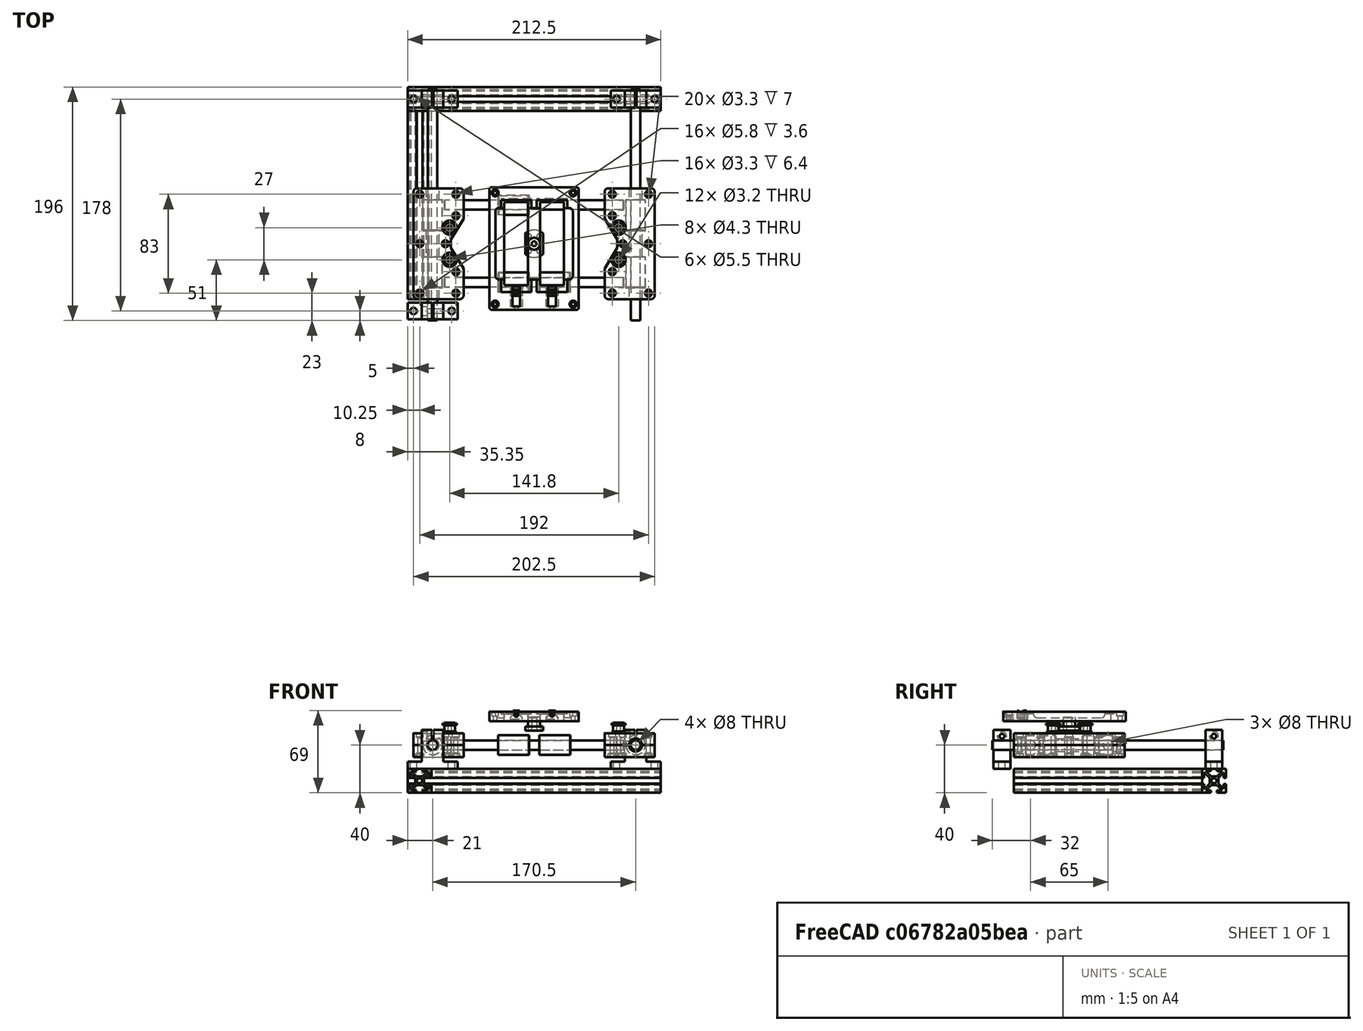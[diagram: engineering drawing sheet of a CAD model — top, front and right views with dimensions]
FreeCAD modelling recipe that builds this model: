
FCSTD DOCUMENT  (FreeCAD 0.16R6706 (Git))
Label: stage3_sh8_alu20
License: All rights reserved
LicenseURL: http://en.wikipedia.org/wiki/All_rights_reserved
objects: Part::FeaturePython×33, Part::Prism×20, Part::Feature×20, Part::Cylinder×19, Part::Extrusion×13, Part::Circle×11, Part::Cut×10, Part::MultiFuse×9, Part::Box×8, Part::Common×6, Part::Compound×5, Part::Fillet×4, Part::Fuse×4, Part::Polygon×2
note: 164 computed .brp shape members not serialized (recipe doc carries the construction recipe); baked Part::Feature solids carry a one-line shape summary decoded from their .brp

FEATURE [Part::Box] topsideslid_box
  Height = 10
  Length = 42
  Placement = pos=(-16,-46.5,0) rot=(0,0,1;0rad)
  Width = 93
FEATURE [Part::Box] bosidetslid_box
  Height = 10
  Length = 42
  Placement = pos=(-16,-46.5,-10) rot=(0,0,1;0rad)
  Width = 93
FEATURE [Part::Fillet] topsideslid_fllt
  Base = -> topsideslid_box
  Edges = 4 edges r=3: [Edge1,Edge3,Edge5,Edge7]
FEATURE [Part::Fillet] botsideslid_fllt
  Base = -> bosidetslid_box
  Edges = 4 edges r=3: [Edge1,Edge3,Edge5,Edge7]
FEATURE [Part::Circle] sliderod_circ
  Angle0 = 0
  Angle1 = 360
  Placement = pos=(0,-47.5,0) rot=(-1,0,0;1.5708rad)
  Radius = 5.5
FEATURE [Part::Extrusion] sliderod
  Base = -> sliderod_circ
  Dir = (0,95,0)
  Solid = true
FEATURE [Part::Cylinder] lm8uu_0_ext
  Angle = 360
  Height = 25
  Placement = pos=(0,-36.5,0) rot=(-1,0,0;1.5708rad)
  Radius = 8
FEATURE [Part::Cylinder] lm8uu_0_int
  Angle = 360
  Height = 27
  Placement = pos=(0,-37.5,0) rot=(-1,0,0;1.5708rad)
  Radius = 4
FEATURE [Part::Cut] lm8uu_0
  Base = -> lm8uu_0_ext
  Tool = -> lm8uu_0_int
FEATURE [Part::Circle] lm8uu_0_cont_circ
  Angle0 = 0
  Angle1 = 360
  Placement = pos=(0,-37,0) rot=(-1,0,0;1.5708rad)
  Radius = 8.35
FEATURE [Part::Extrusion] lm8uu_0_cont
  Base = -> lm8uu_0_cont_circ
  Dir = (0,26,0)
  Solid = true
FEATURE [Part::FeaturePython] Clone  label="lm8uu_1"  # Draft clone (typed FeaturePython)
  Objects = -> [lm8uu_0]
  Placement = pos=(0,48,0) rot=(0,0,1;0rad)
  Scale = (1,1,1)
FEATURE [Part::FeaturePython] Clone001  label="lm8uu_1_cont"  # Draft clone (typed FeaturePython)
  Objects = -> [lm8uu_0_cont]
  Placement = pos=(0,48,0) rot=(0,0,1;0rad)
  Scale = (1,1,1)
FEATURE [Part::Circle] holdrod_0_circ
  Angle0 = 0
  Angle1 = 360
  Placement = pos=(10,0,0) rot=(0,1,0;1.5708rad)
  Radius = 4.175
FEATURE [Part::Extrusion] holdrod_0
  Base = -> holdrod_0_circ
  Dir = (17,0,0)
  Placement = pos=(0,-32.5,0) rot=(0,0,1;0rad)
  Solid = true
FEATURE [Part::Circle] holdrod_1_circ
  Angle0 = 0
  Angle1 = 360
  Placement = pos=(10,0,0) rot=(0,1,0;1.5708rad)
  Radius = 4.175
FEATURE [Part::Extrusion] holdrod_1
  Base = -> holdrod_1_circ
  Dir = (17,0,0)
  Placement = pos=(0,32.5,0) rot=(0,0,1;0rad)
  Solid = true
FEATURE [Part::Cylinder] bolt_hole_bolt_shank
  Angle = 360
  Height = 22
  Placement = pos=(0,0,-1) rot=(0,0,1;0rad)
  Radius = 1.65
FEATURE [Part::Cylinder] bolt_hole_bolt_head
  Angle = 360
  Height = 4.3
  Placement = pos=(0,0,16.7) rot=(0,0,1;0rad)
  Radius = 2.9
FEATURE [Part::Prism] bolt_hole_bolt_sup1
  Circumradius = 3.3
  Height = 3.6
  Placement = pos=(0,0,16.4) rot=(0,0,1;0.523599rad)
  Polygon = 3
FEATURE [Part::Cylinder] bolt_hole_bolt_sup1away
  Angle = 360
  Height = 3.6
  Placement = pos=(0,0,16.4) rot=(0,0,1;0rad)
  Radius = 2.9
FEATURE [Part::Common] sup1cut
  Base = -> bolt_hole_bolt_sup1
  Tool = -> bolt_hole_bolt_sup1away
FEATURE [Part::Prism] bolt_hole_bolt_sup2
  Circumradius = 1.8975
  Height = 3.9
  Placement = pos=(0,0,16.1) rot=(0,0,1;0rad)
  Polygon = 6
FEATURE [Part::MultiFuse] bolt_hole_bolt
  Shapes = -> [bolt_hole_bolt_shank,bolt_hole_bolt_head,sup1cut,bolt_hole_bolt_sup2]
FEATURE [Part::Prism] bolt_hole_nut
  Circumradius = 3.455
  Height = 3.7
  Placement = pos=(0,0,-1) rot=(0,0,1;0rad)
  Polygon = 6
FEATURE [Part::Prism] bolt_hole_nutsup1
  Circumradius = 3.3
  Height = 3
  Placement = pos=(0,0,0) rot=(0,0,1;0.523599rad)
  Polygon = 3
FEATURE [Part::Prism] bolt_hole_supnut1away
  Circumradius = 3.455
  Height = 3
  Polygon = 6
FEATURE [Part::Common] supnut1_cut
  Base = -> bolt_hole_nutsup1
  Tool = -> bolt_hole_supnut1away
FEATURE [Part::Prism] bolt_hole_supnut2
  Circumradius = 1.8975
  Height = 3.3
  Polygon = 6
FEATURE [Part::MultiFuse] boltnut
  Placement = pos=(-10.75,0,-10) rot=(0,0,1;1.5708rad)
  Shapes = -> [bolt_hole_bolt,bolt_hole_nut,supnut1_cut,bolt_hole_supnut2]
FEATURE [Part::FeaturePython] Clone002  label="bolt_hole_r"  # Draft clone (typed FeaturePython)
  Objects = -> [boltnut]
  Placement = pos=(10.75,0,-10) rot=(0,0,1;0.523599rad)
  Scale = (1,1,1)
FEATURE [Part::FeaturePython] Clone003  label="bolt_hole_lu"  # Draft clone (typed FeaturePython)
  Objects = -> [boltnut]
  Placement = pos=(-10.75,-41.5,-10) rot=(0,0,1;0rad)
  Scale = (1,1,1)
FEATURE [Part::FeaturePython] Clone004  label="bolt_hole_ld"  # Draft clone (typed FeaturePython)
  Objects = -> [boltnut]
  Placement = pos=(-10.75,41.5,-10) rot=(0,0,1;0rad)
  Scale = (1,1,1)
FEATURE [Part::FeaturePython] Clone005  label="bolt_hole_ru"  # Draft clone (typed FeaturePython)
  Objects = -> [boltnut]
  Placement = pos=(19.6,41.5,-10) rot=(0,0,1;0rad)
  Scale = (1,1,1)
FEATURE [Part::FeaturePython] Clone006  label="bolt_hole_rd"  # Draft clone (typed FeaturePython)
  Objects = -> [boltnut]
  Placement = pos=(19.6,-41.5,-10) rot=(0,0,1;0rad)
  Scale = (1,1,1)
FEATURE [Part::FeaturePython] Clone007  label="bolt_hole_rmu"  # Draft clone (typed FeaturePython)
  Objects = -> [boltnut]
  Placement = pos=(19.6,23.5,-10) rot=(0,0,1;0rad)
  Scale = (1,1,1)
FEATURE [Part::FeaturePython] Clone008  label="bolt_hole_rmd"  # Draft clone (typed FeaturePython)
  Objects = -> [boltnut]
  Placement = pos=(19.6,-23.5,-10) rot=(0,0,1;0rad)
  Scale = (1,1,1)
FEATURE [Part::Cylinder] boltpul_hole_shank
  Angle = 360
  Height = 22
  Placement = pos=(0,0,-1) rot=(0,0,1;0rad)
  Radius = 1.65
FEATURE [Part::Prism] boltpul_hole_head
  Circumradius = 3.455
  Height = 3.7
  Placement = pos=(0,0,-1) rot=(0,0,1;0rad)
  Polygon = 6
FEATURE [Part::Prism] boltpul_hole_sup1
  Circumradius = 3.3
  Height = 3
  Placement = pos=(0,0,0) rot=(0,0,1;0.523599rad)
  Polygon = 3
FEATURE [Part::Prism] boltpul_hole_sup1away
  Circumradius = 3.455
  Height = 3
  Polygon = 6
FEATURE [Part::Common] sup1cut001
  Base = -> boltpul_hole_sup1
  Tool = -> boltpul_hole_sup1away
FEATURE [Part::Prism] boltpul_hole_sup2
  Circumradius = 1.8975
  Height = 3.3
  Polygon = 6
FEATURE [Part::MultiFuse] boltpul_hole
  Placement = pos=(14.35,13.5,-10) rot=(0,0,1;0.523599rad)
  Shapes = -> [boltpul_hole_shank,boltpul_hole_head,sup1cut001,boltpul_hole_sup2]
FEATURE [Part::Feature] idlepull_01
  shape: bbox 12 x 12 x 1 mm, 4 faces (baked)
FEATURE [Part::Feature] idlepull_02
  shape: bbox 7 x 7 x 0.5 mm, 4 faces (baked)
FEATURE [Part::Feature] idlepull_03
  shape: bbox 9 x 9 x 5 mm, 4 faces (baked)
FEATURE [Part::Feature] idlepull_04
  shape: bbox 7 x 7 x 0.5 mm, 4 faces (baked)
FEATURE [Part::Feature] idlepull_05
  shape: bbox 12 x 12 x 1 mm, 4 faces (baked)
FEATURE [Part::Feature] idlepull_06
  shape: bbox 9 x 9 x 0.8 mm, 4 faces (baked)
FEATURE [Part::Compound] idlepull_0
  Links = -> [idlepull_01,idlepull_02,idlepull_03,idlepull_04,idlepull_05,idlepull_06]
FEATURE [Part::FeaturePython] Clone009  label="boltpul_hole_1"  # Draft clone (typed FeaturePython)
  Objects = -> [boltpul_hole]
  Placement = pos=(14.35,-13.5,-10) rot=(0,0,1;0.523599rad)
  Scale = (1,1,1)
FEATURE [Part::FeaturePython] Clone010  label="idlepull_1"  # Draft clone (typed FeaturePython)
  Objects = -> [idlepull_0]
  Placement = pos=(0,-27,0) rot=(0,0,1;0rad)
  Scale = (1,1,1)
FEATURE [Part::Compound] idlepulls
  Links = -> [idlepull_0,Clone010]
  Placement = pos=(-85.25,0,0) rot=(0,0,1;0rad)
FEATURE [Part::Polygon] dent_plane
  Close = true
  Nodes = (4) [(27,22.5,-11),(15.35,3.5,-11),(15.35,-3.5,-11),(27,-22.5,-11)]
FEATURE [Part::Extrusion] dent
  Base = -> dent_plane
  Dir = (0,0,22)
  Solid = true
FEATURE [Part::MultiFuse] holes
  Shapes = -> [sliderod,lm8uu_0_cont,Clone001,holdrod_0,holdrod_1,boltnut,Clone002,Clone003,Clone004,Clone005,Clone006,Clone007,Clone008,boltpul_hole,Clone009,dent]
FEATURE [Part::Fuse] yslider_nx_bear
  Base = -> lm8uu_0
  Placement = pos=(-85.25,0,0) rot=(0,0,1;0rad)
  Tool = -> Clone
FEATURE [Part::Cut] yslider_nx_top
  Base = -> topsideslid_fllt
  Placement = pos=(-85.25,0,0) rot=(0,0,1;0rad)
  Tool = -> holes
FEATURE [Part::Cut] yslider_nx_bot
  Base = -> botsideslid_fllt
  Placement = pos=(-85.25,0,0) rot=(0,0,1;0rad)
  Tool = -> holes
FEATURE [Part::Feature] alux_y0
  Placement = pos=(0,-56.5,-40) rot=(0,0,1;0rad)
  shape: bbox 212.5 x 20 x 20 mm, 43 faces (baked)
FEATURE [Part::FeaturePython] Clone011  label="alux_y"  # Draft clone (typed FeaturePython)
  Objects = -> [alux_y0]
  Placement = pos=(0,121.5,-40) rot=(0,0,1;0rad)
  Scale = (1,1,1)
FEATURE [Part::Feature] aluy_x
  Placement = pos=(96.25,-46.5,-40) rot=(0,0,1;0rad)
  shape: bbox 20 x 158 x 20 mm, 43 faces (baked)
FEATURE [Part::FeaturePython] Clone012  label="aluy_nx"  # Draft clone (typed FeaturePython)
  Objects = -> [aluy_x]
  Placement = pos=(-96.25,-46.5,-40) rot=(0,0,1;0rad)
  Scale = (1,1,1)
FEATURE [Part::Box] total_box
  Height = 32.8
  Length = 14
  Placement = pos=(0,-21,0) rot=(0,0,1;0rad)
  Width = 42
FEATURE [Part::Box] side_box_r
  Height = 26.8
  Length = 14
  Placement = pos=(0,9,6) rot=(0,0,1;0rad)
  Width = 12
FEATURE [Part::Box] side_box_l
  Height = 26.8
  Length = 14
  Placement = pos=(0,-21,6) rot=(0,0,1;0rad)
  Width = 12
FEATURE [Part::Fuse] side_boxes
  Base = -> side_box_r
  Tool = -> side_box_l
FEATURE [Part::Cut] sk_shape
  Base = -> total_box
  Tool = -> side_boxes
FEATURE [Part::Cylinder] shaft_hole
  Angle = 360
  Height = 16
  Placement = pos=(-1,0,20) rot=(0,1,0;1.5708rad)
  Radius = 4
FEATURE [Part::Box] up_sep
  Height = 13.8
  Length = 16
  Placement = pos=(-1,-0.6,21) rot=(0,0,1;0rad)
  Width = 1.2
FEATURE [Part::Cylinder] tbolt_shaft
  Angle = 360
  Height = 20
  Placement = pos=(7,10,27.5) rot=(1,0,0;1.5708rad)
  Radius = 2
FEATURE [Part::Cylinder] tbolt_head
  Angle = 360
  Height = 5.4
  Placement = pos=(7,10,27.5) rot=(1,0,0;1.5708rad)
  Radius = 3.85
FEATURE [Part::MultiFuse] fuse_shaft_holes
  Shapes = -> [tbolt_head,tbolt_shaft,up_sep,shaft_hole]
FEATURE [Part::Cut] sk_shape_w_holes
  Base = -> sk_shape
  Placement = pos=(0,-7,0) rot=(0,0,1;1.5708rad)
  Tool = -> fuse_shaft_holes
FEATURE [Part::Cylinder] mbolt_sh_r
  Angle = 360
  Height = 8
  Placement = pos=(7,16,-1) rot=(0,0,1;0rad)
  Radius = 2.75
FEATURE [Part::Cylinder] mbolt_sh_l
  Angle = 360
  Height = 8
  Placement = pos=(7,-16,-1) rot=(0,0,1;0rad)
  Radius = 2.75
FEATURE [Part::Fuse] mbolts_sh
  Base = -> mbolt_sh_r
  Placement = pos=(0,-7,0) rot=(0,0,1;1.5708rad)
  Tool = -> mbolt_sh_l
FEATURE [Part::Cut] sky_x_y0
  Base = -> sk_shape_w_holes
  Placement = pos=(85.25,-56.5,-20) rot=(0,0,1;0rad)
  Tool = -> mbolts_sh
FEATURE [Part::FeaturePython] Clone013  label="sky_nx_y0"  # Draft clone (typed FeaturePython)
  Objects = -> [sky_x_y0]
  Placement = pos=(-85.25,-56.5,-20) rot=(0,0,1;0rad)
  Scale = (1,1,1)
FEATURE [Part::FeaturePython] Clone014  label="sky_x_y"  # Draft clone (typed FeaturePython)
  Objects = -> [sky_x_y0]
  Placement = pos=(85.25,121.5,-20) rot=(0,0,1;0rad)
  Scale = (1,1,1)
FEATURE [Part::FeaturePython] Clone015  label="sky_nx_y"  # Draft clone (typed FeaturePython)
  Objects = -> [sky_x_y0]
  Placement = pos=(-85.25,121.5,-20) rot=(0,0,1;0rad)
  Scale = (1,1,1)
FEATURE [Part::Feature] rody_x
  shape: bbox 8 x 194 x 8 mm, 3 faces (baked)
FEATURE [Part::Feature] rody_nx
  shape: bbox 8 x 194 x 8 mm, 3 faces (baked)
FEATURE [Part::Box] topsideslid_box001
  Height = 10
  Length = 42
  Placement = pos=(-16,-46.5,0) rot=(0,0,1;0rad)
  Width = 93
FEATURE [Part::Box] bosidetslid_box001
  Height = 10
  Length = 42
  Placement = pos=(-16,-46.5,-10) rot=(0,0,1;0rad)
  Width = 93
FEATURE [Part::Fillet] topsideslid_fllt001
  Base = -> topsideslid_box001
  Edges = 4 edges r=3: [Edge1,Edge3,Edge5,Edge7]
  Placement = pos=(0,0,0) rot=(0,0,1;3.14159rad)
FEATURE [Part::Fillet] botsideslid_fllt001
  Base = -> bosidetslid_box001
  Edges = 4 edges r=3: [Edge1,Edge3,Edge5,Edge7]
  Placement = pos=(0,0,0) rot=(0,0,1;3.14159rad)
FEATURE [Part::Circle] sliderod_circ001
  Angle0 = 0
  Angle1 = 360
  Placement = pos=(0,-47.5,0) rot=(-1,0,0;1.5708rad)
  Radius = 5.5
FEATURE [Part::Extrusion] sliderod001
  Base = -> sliderod_circ001
  Dir = (0,95,0)
  Solid = true
FEATURE [Part::Cylinder] lm8uu_0_ext001
  Angle = 360
  Height = 25
  Placement = pos=(0,-36.5,0) rot=(-1,0,0;1.5708rad)
  Radius = 8
FEATURE [Part::Cylinder] lm8uu_0_int001
  Angle = 360
  Height = 27
  Placement = pos=(0,-37.5,0) rot=(-1,0,0;1.5708rad)
  Radius = 4
FEATURE [Part::Cut] lm8uu_0001
  Base = -> lm8uu_0_ext001
  Tool = -> lm8uu_0_int001
FEATURE [Part::Circle] lm8uu_0_cont_circ001
  Angle0 = 0
  Angle1 = 360
  Placement = pos=(0,-37,0) rot=(-1,0,0;1.5708rad)
  Radius = 8.35
FEATURE [Part::Extrusion] lm8uu_0_cont001
  Base = -> lm8uu_0_cont_circ001
  Dir = (0,26,0)
  Solid = true
FEATURE [Part::FeaturePython] Clone016  label="lm8uu_0002"  # Draft clone (typed FeaturePython)
  Objects = -> [lm8uu_0001]
  Placement = pos=(0,48,0) rot=(0,0,1;0rad)
  Scale = (1,1,1)
FEATURE [Part::FeaturePython] Clone017  label="lm8uu_1_cont001"  # Draft clone (typed FeaturePython)
  Objects = -> [lm8uu_0_cont001]
  Placement = pos=(0,48,0) rot=(0,0,1;0rad)
  Scale = (1,1,1)
FEATURE [Part::Circle] holdrod_0_circ001
  Angle0 = 0
  Angle1 = 360
  Placement = pos=(10,0,0) rot=(0,1,0;1.5708rad)
  Radius = 4.175
FEATURE [Part::Extrusion] holdrod_0001
  Base = -> holdrod_0_circ001
  Dir = (17,0,0)
  Placement = pos=(0,-32.5,0) rot=(0,0,1;0rad)
  Solid = true
FEATURE [Part::Circle] holdrod_1_circ001
  Angle0 = 0
  Angle1 = 360
  Placement = pos=(10,0,0) rot=(0,1,0;1.5708rad)
  Radius = 4.175
FEATURE [Part::Extrusion] holdrod_1001
  Base = -> holdrod_1_circ001
  Dir = (17,0,0)
  Placement = pos=(0,32.5,0) rot=(0,0,1;0rad)
  Solid = true
FEATURE [Part::Cylinder] bolt_hole_bolt_shank001
  Angle = 360
  Height = 22
  Placement = pos=(0,0,-1) rot=(0,0,1;0rad)
  Radius = 1.65
FEATURE [Part::Cylinder] bolt_hole_bolt_head001
  Angle = 360
  Height = 4.3
  Placement = pos=(0,0,16.7) rot=(0,0,1;0rad)
  Radius = 2.9
FEATURE [Part::Prism] bolt_hole_bolt_sup1001
  Circumradius = 3.3
  Height = 3.6
  Placement = pos=(0,0,16.4) rot=(0,0,1;0.523599rad)
  Polygon = 3
FEATURE [Part::Cylinder] bolt_hole_bolt_sup1away001
  Angle = 360
  Height = 3.6
  Placement = pos=(0,0,16.4) rot=(0,0,1;0rad)
  Radius = 2.9
FEATURE [Part::Common] sup1cut002
  Base = -> bolt_hole_bolt_sup1001
  Tool = -> bolt_hole_bolt_sup1away001
FEATURE [Part::Prism] bolt_hole_bolt_sup2001
  Circumradius = 1.8975
  Height = 3.9
  Placement = pos=(0,0,16.1) rot=(0,0,1;0rad)
  Polygon = 6
FEATURE [Part::MultiFuse] bolt_hole_bolt001
  Shapes = -> [bolt_hole_bolt_shank001,bolt_hole_bolt_head001,sup1cut002,bolt_hole_bolt_sup2001]
FEATURE [Part::Prism] bolt_hole_nut001
  Circumradius = 3.455
  Height = 3.7
  Placement = pos=(0,0,-1) rot=(0,0,1;0rad)
  Polygon = 6
FEATURE [Part::Prism] bolt_hole_nutsup1001
  Circumradius = 3.3
  Height = 3
  Placement = pos=(0,0,0) rot=(0,0,1;0.523599rad)
  Polygon = 3
FEATURE [Part::Prism] bolt_hole_supnut1away001
  Circumradius = 3.455
  Height = 3
  Polygon = 6
FEATURE [Part::Common] supnut1_cut001
  Base = -> bolt_hole_nutsup1001
  Tool = -> bolt_hole_supnut1away001
FEATURE [Part::Prism] bolt_hole_supnut2001
  Circumradius = 1.8975
  Height = 3.3
  Polygon = 6
FEATURE [Part::MultiFuse] boltnut001
  Placement = pos=(-10.75,0,-10) rot=(0,0,1;1.5708rad)
  Shapes = -> [bolt_hole_bolt001,bolt_hole_nut001,supnut1_cut001,bolt_hole_supnut2001]
FEATURE [Part::FeaturePython] Clone018  label="bolt_hole_r001"  # Draft clone (typed FeaturePython)
  Objects = -> [boltnut001]
  Placement = pos=(10.75,0,-10) rot=(0,0,1;0.523599rad)
  Scale = (1,1,1)
FEATURE [Part::FeaturePython] Clone019  label="bolt_hole_lu001"  # Draft clone (typed FeaturePython)
  Objects = -> [boltnut001]
  Placement = pos=(-10.75,-41.5,-10) rot=(0,0,1;0rad)
  Scale = (1,1,1)
FEATURE [Part::FeaturePython] Clone020  label="bolt_hole_ld001"  # Draft clone (typed FeaturePython)
  Objects = -> [boltnut001]
  Placement = pos=(-10.75,41.5,-10) rot=(0,0,1;0rad)
  Scale = (1,1,1)
FEATURE [Part::FeaturePython] Clone021  label="bolt_hole_ru001"  # Draft clone (typed FeaturePython)
  Objects = -> [boltnut001]
  Placement = pos=(19.6,41.5,-10) rot=(0,0,1;0rad)
  Scale = (1,1,1)
FEATURE [Part::FeaturePython] Clone022  label="bolt_hole_rd001"  # Draft clone (typed FeaturePython)
  Objects = -> [boltnut001]
  Placement = pos=(19.6,-41.5,-10) rot=(0,0,1;0rad)
  Scale = (1,1,1)
FEATURE [Part::FeaturePython] Clone023  label="bolt_hole_rmu001"  # Draft clone (typed FeaturePython)
  Objects = -> [boltnut001]
  Placement = pos=(19.6,23.5,-10) rot=(0,0,1;0rad)
  Scale = (1,1,1)
FEATURE [Part::FeaturePython] Clone024  label="bolt_hole_rmd001"  # Draft clone (typed FeaturePython)
  Objects = -> [boltnut001]
  Placement = pos=(19.6,-23.5,-10) rot=(0,0,1;0rad)
  Scale = (1,1,1)
FEATURE [Part::Cylinder] boltpul_hole_shank001
  Angle = 360
  Height = 22
  Placement = pos=(0,0,-1) rot=(0,0,1;0rad)
  Radius = 1.65
FEATURE [Part::Prism] boltpul_hole_head001
  Circumradius = 3.455
  Height = 3.7
  Placement = pos=(0,0,-1) rot=(0,0,1;0rad)
  Polygon = 6
FEATURE [Part::Prism] boltpul_hole_sup1001
  Circumradius = 3.3
  Height = 3
  Placement = pos=(0,0,0) rot=(0,0,1;0.523599rad)
  Polygon = 3
FEATURE [Part::Prism] boltpul_hole_sup1away001
  Circumradius = 3.455
  Height = 3
  Polygon = 6
FEATURE [Part::Common] sup1cut003
  Base = -> boltpul_hole_sup1001
  Tool = -> boltpul_hole_sup1away001
FEATURE [Part::Prism] boltpul_hole_sup2001
  Circumradius = 1.8975
  Height = 3.3
  Polygon = 6
FEATURE [Part::MultiFuse] boltpul_hole001
  Placement = pos=(14.35,13.5,-10) rot=(0,0,1;0.523599rad)
  Shapes = -> [boltpul_hole_shank001,boltpul_hole_head001,sup1cut003,boltpul_hole_sup2001]
FEATURE [Part::Feature] idlepull_01001
  shape: bbox 12 x 12 x 1 mm, 4 faces (baked)
FEATURE [Part::Feature] idlepull_02001
  shape: bbox 7 x 7 x 0.5 mm, 4 faces (baked)
FEATURE [Part::Feature] idlepull_03001
  shape: bbox 9 x 9 x 5 mm, 4 faces (baked)
FEATURE [Part::Feature] idlepull_04001
  shape: bbox 7 x 7 x 0.5 mm, 4 faces (baked)
FEATURE [Part::Feature] idlepull_05001
  shape: bbox 12 x 12 x 1 mm, 4 faces (baked)
FEATURE [Part::Feature] idlepull_06001
  shape: bbox 9 x 9 x 0.8 mm, 4 faces (baked)
FEATURE [Part::Compound] idlepull_06002
  Links = -> [idlepull_01001,idlepull_02001,idlepull_03001,idlepull_04001,idlepull_05001,idlepull_06001]
FEATURE [Part::FeaturePython] Clone025  label="boltpul_hole_002"  # Draft clone (typed FeaturePython)
  Objects = -> [boltpul_hole001]
  Placement = pos=(14.35,-13.5,-10) rot=(0,0,1;0.523599rad)
  Scale = (1,1,1)
FEATURE [Part::FeaturePython] Clone026  label="idlepull_06003"  # Draft clone (typed FeaturePython)
  Objects = -> [idlepull_06002]
  Placement = pos=(0,-27,0) rot=(0,0,1;0rad)
  Scale = (1,1,1)
FEATURE [Part::Compound] idlepulls001
  Links = -> [idlepull_06002,Clone026]
  Placement = pos=(85.25,0,0) rot=(0,0,1;3.14159rad)
FEATURE [Part::Polygon] dent_plane001
  Close = true
  Nodes = (4) [(27,22.5,-11),(15.35,3.5,-11),(15.35,-3.5,-11),(27,-22.5,-11)]
FEATURE [Part::Extrusion] dent001
  Base = -> dent_plane001
  Dir = (0,0,22)
  Solid = true
FEATURE [Part::MultiFuse] holes001
  Placement = pos=(0,0,0) rot=(0,0,1;3.14159rad)
  Shapes = -> [sliderod001,lm8uu_0_cont001,Clone017,holdrod_0001,holdrod_1001,boltnut001,Clone018,Clone019,Clone020,Clone021,Clone022,Clone023,Clone024,boltpul_hole001,Clone025,dent001]
FEATURE [Part::Fuse] yslider_x_bear
  Base = -> lm8uu_0001
  Placement = pos=(85.25,0,0) rot=(0,0,1;0rad)
  Tool = -> Clone016
FEATURE [Part::Cut] yslider_x_top
  Base = -> topsideslid_fllt001
  Placement = pos=(85.25,0,0) rot=(0,0,1;0rad)
  Tool = -> holes001
FEATURE [Part::Cut] yslider_x_bot
  Base = -> botsideslid_fllt001
  Placement = pos=(85.25,0,0) rot=(0,0,1;0rad)
  Tool = -> holes001
FEATURE [Part::Circle] rod_x_ny_circ
  Angle0 = 0
  Angle1 = 360
  Placement = pos=(-74.85,0,0) rot=(0,1,0;1.5708rad)
  Radius = 4
FEATURE [Part::Extrusion] rod_x_ny
  Base = -> rod_x_ny_circ
  Dir = (149.7,0,0)
  Placement = pos=(0,-32.5,0) rot=(0,0,1;0rad)
  Solid = true
FEATURE [Part::Circle] rod_x_y_circ
  Angle0 = 0
  Angle1 = 360
  Placement = pos=(-74.85,0,0) rot=(0,1,0;1.5708rad)
  Radius = 4
FEATURE [Part::Extrusion] rod_x_y
  Base = -> rod_x_y_circ
  Dir = (149.7,0,0)
  Placement = pos=(0,32.5,0) rot=(0,0,1;0rad)
  Solid = true
FEATURE [Part::Cylinder] lm8uu_cen_x_y_ext
  Angle = 360
  Height = 25
  Placement = pos=(-12.5,0,0) rot=(0,1,0;1.5708rad)
  Radius = 8
FEATURE [Part::Cylinder] lm8uu_cen_x_y_int
  Angle = 360
  Height = 27
  Placement = pos=(-13.5,0,0) rot=(0,1,0;1.5708rad)
  Radius = 4
FEATURE [Part::Cut] lm8uu_cen_x_y
  Base = -> lm8uu_cen_x_y_ext
  Placement = pos=(17.25,32.5,0) rot=(0,0,1;0rad)
  Tool = -> lm8uu_cen_x_y_int
FEATURE [Part::Circle] lm8uu_cen_x_y_cont_circ
  Angle0 = 0
  Angle1 = 360
  Placement = pos=(-13,0,0) rot=(0,1,0;1.5708rad)
  Radius = 8.35
FEATURE [Part::Extrusion] lm8uu_cen_x_y_cont
  Base = -> lm8uu_cen_x_y_cont_circ
  Dir = (26,0,0)
  Placement = pos=(17.25,32.5,0) rot=(0,0,1;0rad)
  Solid = true
FEATURE [Part::FeaturePython] Clone027  label="lm8uu_cen_nx_y"  # Draft clone (typed FeaturePython)
  Objects = -> [lm8uu_cen_x_y]
  Placement = pos=(-17.25,32.5,0) rot=(0,0,1;0rad)
  Scale = (1,1,1)
FEATURE [Part::FeaturePython] Clone028  label="lm8uu_cen_nx_y_cont"  # Draft clone (typed FeaturePython)
  Objects = -> [lm8uu_cen_x_y_cont]
  Placement = pos=(-17.25,32.5,0) rot=(0,0,1;0rad)
  Scale = (1,1,1)
FEATURE [Part::FeaturePython] Clone029  label="lm8uu_cen_x_ny"  # Draft clone (typed FeaturePython)
  Objects = -> [lm8uu_cen_x_y]
  Placement = pos=(17.25,-32.5,0) rot=(0,0,1;0rad)
  Scale = (1,1,1)
FEATURE [Part::FeaturePython] Clone030  label="lm8uu_cen_x_ny_cont"  # Draft clone (typed FeaturePython)
  Objects = -> [lm8uu_cen_x_y_cont]
  Placement = pos=(17.25,-32.5,0) rot=(0,0,1;0rad)
  Scale = (1,1,1)
FEATURE [Part::FeaturePython] Clone031  label="lm8uu_cen_nx_ny"  # Draft clone (typed FeaturePython)
  Objects = -> [lm8uu_cen_x_y]
  Placement = pos=(-17.25,-32.5,0) rot=(0,0,1;0rad)
  Scale = (1,1,1)
FEATURE [Part::FeaturePython] Clone032  label="lm8uu_cen_nx_ny_cont"  # Draft clone (typed FeaturePython)
  Objects = -> [lm8uu_cen_x_y_cont]
  Placement = pos=(-17.25,-32.5,0) rot=(0,0,1;0rad)
  Scale = (1,1,1)
FEATURE [Part::Feature] portatray
  shape: bbox 75 x 103 x 8 mm, 105 faces (baked)
FEATURE [Part::Feature] portatrayclamp_0
  shape: bbox 10 x 8 x 7 mm, 19 faces (baked)
FEATURE [Part::Feature] portatrayclamp_1
  shape: bbox 10 x 8 x 7 mm, 19 faces (baked)
FEATURE [Part::Compound] portatray_clamp
  Links = -> [portatrayclamp_0,portatrayclamp_1]
FEATURE [Part::Feature] vertical_lscrew_nut
  shape: bbox 15 x 23 x 11.5 mm, 13 faces (baked)
